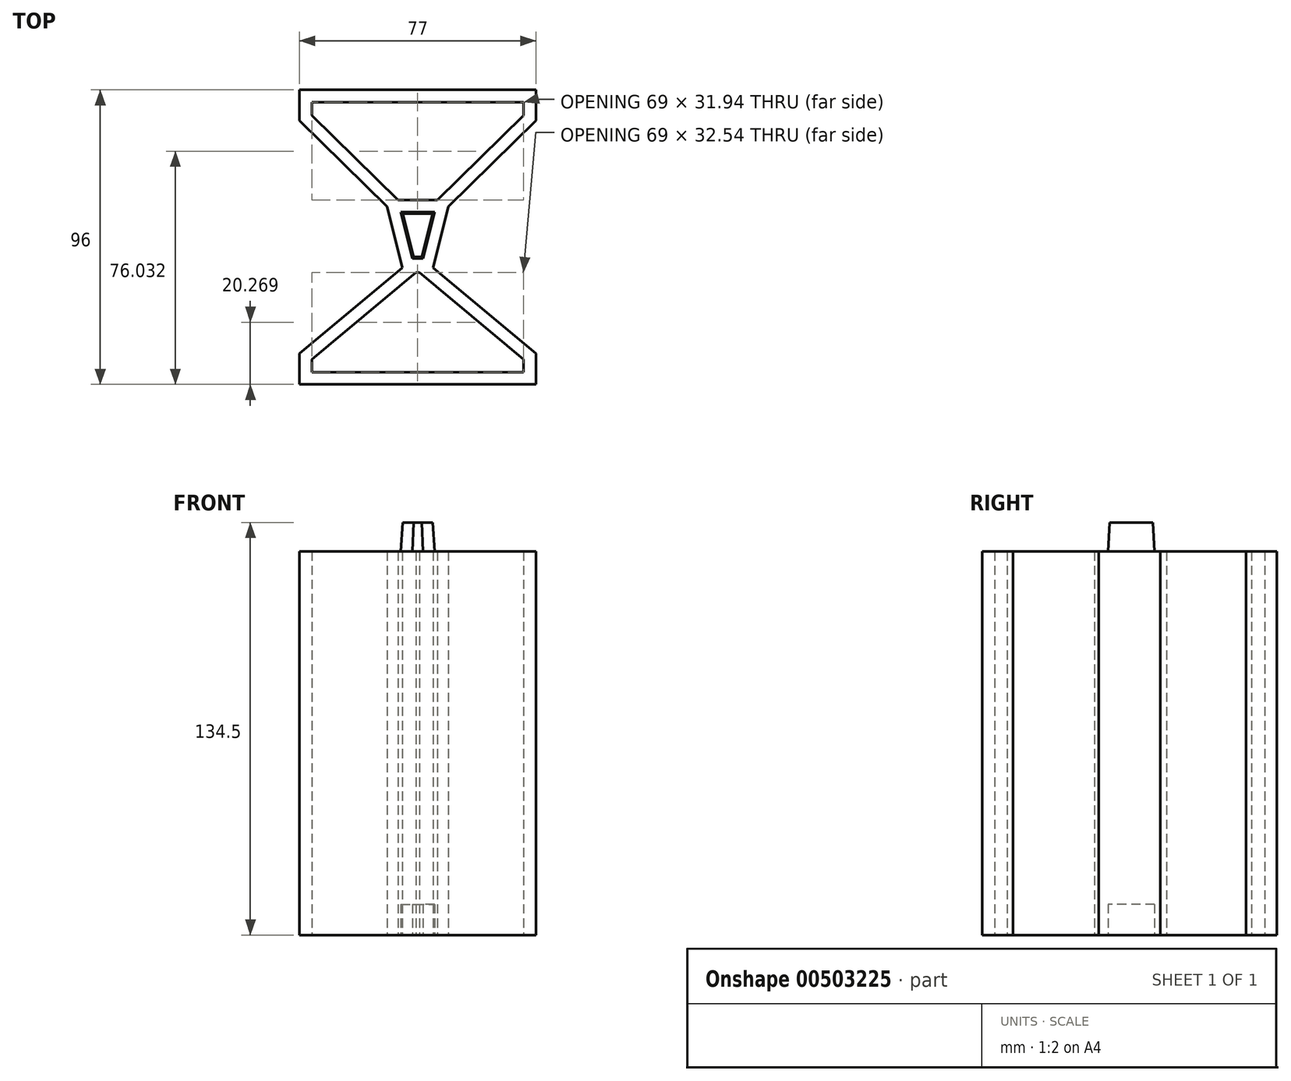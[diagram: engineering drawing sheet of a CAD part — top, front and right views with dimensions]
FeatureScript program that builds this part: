
annotation { "Feature Type Name" : "Feature", "Feature Type Description" : "" }
export const myFeature = defineFeature(function(context is Context, id is Id, definition is map)
    precondition{}
    {
        {
            var Q0;
            Q0=qCreatedBy(makeId("Top.planeOp"),FACE);
            var sketch = newSketch(context, id + "F0", { "sketchPlane" : qUnion([Q0])});
            skLineSegment(sketch, "E0", {"start": v(-38.5, -48) * mm, "end": v(38.5, -48) * mm});
            skLineSegment(sketch, "E1", {"start": v(0, -48) * mm, "end": v(0, 48) * mm, "construction": true});
            skLineSegment(sketch, "E2", {"start": v(-38.5, 48) * mm, "end": v(38.5, 48) * mm});
            skPoint(sketch, "E3", {"position": v(0, 48) * mm});
            skPoint(sketch, "E4", {"position": v(0, 0) * mm});
            skLineSegment(sketch, "E5.0", {"start": v(-38.5, -51) * mm, "end": v(38.5, -51) * mm});
            skLineSegment(sketch, "E6", {"start": v(-38.5, -51) * mm, "end": v(-38.5, -48) * mm});
            skLineSegment(sketch, "E7", {"start": v(38.5, -51) * mm, "end": v(38.5, -48) * mm});
            skLineSegment(sketch, "E8.0", {"start": v(-38.5, 51) * mm, "end": v(38.5, 51) * mm});
            skLineSegment(sketch, "E9", {"start": v(-38.5, 51) * mm, "end": v(-38.5, 48) * mm});
            skLineSegment(sketch, "E10", {"start": v(38.5, 51) * mm, "end": v(38.5, 48) * mm});
            skLineSegment(sketch, "E11", {"start": v(-38.5, -48) * mm, "end": v(-38.5, -38) * mm});
            skLineSegment(sketch, "E12", {"start": v(0, 0) * mm, "end": v(0, -10) * mm, "construction": true});
            skLineSegment(sketch, "E13", {"start": v(0, -10) * mm, "end": v(-5, -10) * mm, "construction": true});
            skLineSegment(sketch, "E14", {"start": v(-5, -10) * mm, "end": v(-38.5, -38) * mm});
            skLineSegment(sketch, "E15", {"start": v(-38.5, 48) * mm, "end": v(-38.5, 38) * mm});
            skLineSegment(sketch, "E16", {"start": v(0, 0) * mm, "end": v(0, 10) * mm, "construction": true});
            skLineSegment(sketch, "E17", {"start": v(0, 10) * mm, "end": v(-10, 10) * mm, "construction": true});
            skLineSegment(sketch, "E18", {"start": v(-10, 10) * mm, "end": v(-38.5, 38) * mm});
            skLineSegment(sketch, "E19", {"start": v(-10, 10) * mm, "end": v(-5, -10) * mm});
            skLineSegment(sketch, "E20.MirrorCS", {"start": v(38.5, 48) * mm, "end": v(38.5, 38) * mm});
            skLineSegment(sketch, "E21.MirrorCS", {"start": v(10, 10) * mm, "end": v(38.5, 38) * mm});
            skLineSegment(sketch, "E22.MirrorCS", {"start": v(10, 10) * mm, "end": v(5, -10) * mm});
            skLineSegment(sketch, "E23.MirrorCS", {"start": v(5, -10) * mm, "end": v(38.5, -38) * mm});
            skLineSegment(sketch, "E24.MirrorCS", {"start": v(38.5, -48) * mm, "end": v(38.5, -38) * mm});
            skLineSegment(sketch, "E25.1", {"start": v(0.51, -11.46) * mm, "end": v(34.5, -39.87) * mm});
            skLineSegment(sketch, "E25.2", {"start": v(34.5, -44) * mm, "end": v(34.5, -39.87) * mm});
            skLineSegment(sketch, "E25.3", {"start": v(-34.5, -44) * mm, "end": v(34.5, -44) * mm});
            skLineSegment(sketch, "E25.4", {"start": v(-34.5, -44) * mm, "end": v(-34.5, -39.87) * mm});
            skLineSegment(sketch, "E25.6", {"start": v(-0.51, -11.46) * mm, "end": v(-34.5, -39.87) * mm});
            skLineSegment(sketch, "E25.7", {"start": v(6.4, 12.06) * mm, "end": v(34.5, 39.68) * mm});
            skLineSegment(sketch, "E25.8", {"start": v(34.5, 44) * mm, "end": v(34.5, 39.68) * mm});
            skLineSegment(sketch, "E25.9", {"start": v(-34.5, 44) * mm, "end": v(34.5, 44) * mm});
            skLineSegment(sketch, "E25.10", {"start": v(-34.5, 44) * mm, "end": v(-34.5, 39.68) * mm});
            skLineSegment(sketch, "E25.11", {"start": v(-6.4, 12.06) * mm, "end": v(-34.5, 39.68) * mm});
            skLineSegment(sketch, "E26", {"start": v(-6.4, 12.06) * mm, "end": v(6.4, 12.06) * mm});
            skLineSegment(sketch, "E27", {"start": v(-0.51, -11.46) * mm, "end": v(0.51, -11.46) * mm});
            skLineSegment(sketch, "E28.1", {"start": v(5.52, 8.16) * mm, "end": v(1.74, -6.96) * mm});
            skLineSegment(sketch, "E28.3", {"start": v(-5.52, 8.16) * mm, "end": v(-1.74, -6.96) * mm});
            skLineSegment(sketch, "E28.4", {"start": v(-5.52, 8.16) * mm, "end": v(5.52, 8.16) * mm});
            skLineSegment(sketch, "E29", {"start": v(-5.52, 8.16) * mm, "end": v(-5.52, 12.06) * mm, "construction": true});
            skLineSegment(sketch, "E30", {"start": v(5.52, 8.16) * mm, "end": v(5.52, 12.06) * mm, "construction": true});
            skLineSegment(sketch, "E31", {"start": v(0, 8.16) * mm, "end": v(0, 0) * mm, "construction": true});
            skLineSegment(sketch, "E32", {"start": v(-38.5, 38) * mm, "end": v(-38.5, -38) * mm, "construction": true});
            skLineSegment(sketch, "E33", {"start": v(0, 0) * mm, "end": v(0, -11.46) * mm, "construction": true});
            skLineSegment(sketch, "E34", {"start": v(0, -11.46) * mm, "end": v(0, -44) * mm, "construction": true});
            skLineSegment(sketch, "E35", {"start": v(-1.74, -6.96) * mm, "end": v(1.74, -6.96) * mm});
            skLineSegment(sketch, "E36", {"start": v(0, 0) * mm, "end": v(0, -6.96) * mm, "construction": true});
            skSolve(sketch);
        }
        {
            var Q0;
            Q0=makeQuery(id+"F0.imprint","IMPRINT",FACE,{"disambiguationData":[TD([[makeQuery(id+"F0.imprint","IMPRINT",EDGE,{"derivedFrom":sQuery(id+"F0.wireOp",EDGE,"E0")}),1.0]])]});
            var Q1;
            Q1=makeQuery(id+"F0.imprint","IMPRINT",FACE,{"disambiguationData":[TD([[makeQuery(id+"F0.imprint","IMPRINT",EDGE,{"derivedFrom":sQuery(id+"F0.wireOp",EDGE,"E19")}),1.0]])]});
            var Q2;
            Q2=makeQuery(id+"F0.imprint","IMPRINT",FACE,{"disambiguationData":[TD([[makeQuery(id+"F0.imprint","IMPRINT",EDGE,{"derivedFrom":sQuery(id+"F0.wireOp",EDGE,"E2")}),-1.0]])]});
            var Q3;
            Q3=makeQuery(id+"F0.imprint","IMPRINT",FACE,{"disambiguationData":[TD([[makeQuery(id+"F0.imprint","IMPRINT",EDGE,{"derivedFrom":sQuery(id+"F0.wireOp",EDGE,"E28.0")}),-1.0]])]});
            var Q4;
            Q4=makeQuery(id+"F0.imprint","IMPRINT",FACE,{"disambiguationData":[TD([[makeQuery(id+"F0.imprint","IMPRINT",EDGE,{"derivedFrom":sQuery(id+"F0.wireOp",EDGE,"E28.1")}),-1.0]])]});
            extrude(context, id + "F1", {"entities" : qUnion([Q0, Q1, Q2, Q3, Q4]), "depth" : 125 * mm});
        }
        {
            var Q0;
            Q0=makeQuery(id+"F0.imprint","IMPRINT",FACE,{"disambiguationData":[TD([[makeQuery(id+"F0.imprint","IMPRINT",EDGE,{"derivedFrom":sQuery(id+"F0.wireOp",EDGE,"E28.0")}),-1.0]])]});
            var Q1;
            Q1=makeQuery(id+"F0.imprint","IMPRINT",FACE,{"disambiguationData":[TD([[makeQuery(id+"F0.imprint","IMPRINT",EDGE,{"derivedFrom":sQuery(id+"F0.wireOp",EDGE,"E28.1")}),-1.0]])]});
            extrude(context, id + "F2", {"entities" : qUnion([Q0, Q1]), "operationType" : NewBodyOperationType.REMOVE, "depth" : 10 * mm});
        }
        {
            var Q0;
            Q0=makeQuery(id+"F1.opExtrude","CAP_FACE",FACE,{"disambiguationData":[OSD([sQuery(id+"F0.wireOp",EDGE,"E0"),sQuery(id+"F0.wireOp",EDGE,"E2"),sQuery(id+"F0.wireOp",EDGE,"E11"),sQuery(id+"F0.wireOp",EDGE,"E14"),sQuery(id+"F0.wireOp",EDGE,"E15"),sQuery(id+"F0.wireOp",EDGE,"E18"),sQuery(id+"F0.wireOp",EDGE,"E19"),sQuery(id+"F0.wireOp",EDGE,"E20.MirrorCS"),sQuery(id+"F0.wireOp",EDGE,"E21.MirrorCS"),sQuery(id+"F0.wireOp",EDGE,"E22.MirrorCS"),sQuery(id+"F0.wireOp",EDGE,"E23.MirrorCS"),sQuery(id+"F0.wireOp",EDGE,"E24.MirrorCS"),sQuery(id+"F0.wireOp",EDGE,"E25.1"),sQuery(id+"F0.wireOp",EDGE,"E25.2"),sQuery(id+"F0.wireOp",EDGE,"E25.3"),sQuery(id+"F0.wireOp",EDGE,"E25.4"),sQuery(id+"F0.wireOp",EDGE,"E25.6"),sQuery(id+"F0.wireOp",EDGE,"E25.7"),sQuery(id+"F0.wireOp",EDGE,"E25.8"),sQuery(id+"F0.wireOp",EDGE,"E25.9"),sQuery(id+"F0.wireOp",EDGE,"E25.10"),sQuery(id+"F0.wireOp",EDGE,"E25.11"),sQuery(id+"F0.wireOp",EDGE,"E26"),sQuery(id+"F0.wireOp",EDGE,"E27")])],"isStart":false});
            var sketch = newSketch(context, id + "F3", { "sketchPlane" : qUnion([Q0])});
            skLineSegment(sketch, "E37", {"start": v(-38.5, -48) * mm, "end": v(38.5, -48) * mm});
            skLineSegment(sketch, "E38", {"start": v(0, -48) * mm, "end": v(0, 48) * mm, "construction": true});
            skLineSegment(sketch, "E39", {"start": v(-38.5, 48) * mm, "end": v(38.5, 48) * mm});
            skPoint(sketch, "E40", {"position": v(0, 48) * mm});
            skPoint(sketch, "E41", {"position": v(0, 0) * mm});
            skLineSegment(sketch, "E42.0", {"start": v(-38.5, -51) * mm, "end": v(38.5, -51) * mm});
            skLineSegment(sketch, "E43", {"start": v(-38.5, -51) * mm, "end": v(-38.5, -48) * mm});
            skLineSegment(sketch, "E44", {"start": v(38.5, -51) * mm, "end": v(38.5, -48) * mm});
            skLineSegment(sketch, "E45.0", {"start": v(-38.5, 51) * mm, "end": v(38.5, 51) * mm});
            skLineSegment(sketch, "E46", {"start": v(-38.5, 51) * mm, "end": v(-38.5, 48) * mm});
            skLineSegment(sketch, "E47", {"start": v(38.5, 51) * mm, "end": v(38.5, 48) * mm});
            skLineSegment(sketch, "E48", {"start": v(-38.5, -48) * mm, "end": v(-38.5, -38) * mm});
            skLineSegment(sketch, "E49", {"start": v(0, 0) * mm, "end": v(0, -10) * mm, "construction": true});
            skLineSegment(sketch, "E50", {"start": v(0, -10) * mm, "end": v(-5, -10) * mm, "construction": true});
            skLineSegment(sketch, "E51", {"start": v(-5, -10) * mm, "end": v(-38.5, -38) * mm});
            skLineSegment(sketch, "E52", {"start": v(-38.5, 48) * mm, "end": v(-38.5, 38) * mm});
            skLineSegment(sketch, "E53", {"start": v(0, 0) * mm, "end": v(0, 10) * mm, "construction": true});
            skLineSegment(sketch, "E54", {"start": v(0, 10) * mm, "end": v(-10, 10) * mm, "construction": true});
            skLineSegment(sketch, "E55", {"start": v(-10, 10) * mm, "end": v(-38.5, 38) * mm});
            skLineSegment(sketch, "E56", {"start": v(-10, 10) * mm, "end": v(-5, -10) * mm});
            skLineSegment(sketch, "E57.MirrorCS", {"start": v(38.5, 48) * mm, "end": v(38.5, 38) * mm});
            skLineSegment(sketch, "E58.MirrorCS", {"start": v(10, 10) * mm, "end": v(38.5, 38) * mm});
            skLineSegment(sketch, "E59.MirrorCS", {"start": v(10, 10) * mm, "end": v(5, -10) * mm});
            skLineSegment(sketch, "E60.MirrorCS", {"start": v(5, -10) * mm, "end": v(38.5, -38) * mm});
            skLineSegment(sketch, "E61.MirrorCS", {"start": v(38.5, -48) * mm, "end": v(38.5, -38) * mm});
            skLineSegment(sketch, "E62.1", {"start": v(0.51, -11.46) * mm, "end": v(34.5, -39.87) * mm});
            skLineSegment(sketch, "E62.2", {"start": v(34.5, -44) * mm, "end": v(34.5, -39.87) * mm});
            skLineSegment(sketch, "E62.3", {"start": v(-34.5, -44) * mm, "end": v(34.5, -44) * mm});
            skLineSegment(sketch, "E62.4", {"start": v(-34.5, -44) * mm, "end": v(-34.5, -39.87) * mm});
            skLineSegment(sketch, "E62.6", {"start": v(-0.51, -11.46) * mm, "end": v(-34.5, -39.87) * mm});
            skLineSegment(sketch, "E62.7", {"start": v(6.4, 12.06) * mm, "end": v(34.5, 39.68) * mm});
            skLineSegment(sketch, "E62.8", {"start": v(34.5, 44) * mm, "end": v(34.5, 39.68) * mm});
            skLineSegment(sketch, "E62.9", {"start": v(-34.5, 44) * mm, "end": v(34.5, 44) * mm});
            skLineSegment(sketch, "E62.10", {"start": v(-34.5, 44) * mm, "end": v(-34.5, 39.68) * mm});
            skLineSegment(sketch, "E62.11", {"start": v(-6.4, 12.06) * mm, "end": v(-34.5, 39.68) * mm});
            skLineSegment(sketch, "E63", {"start": v(-6.4, 12.06) * mm, "end": v(6.4, 12.06) * mm});
            skLineSegment(sketch, "E64", {"start": v(-0.51, -11.46) * mm, "end": v(0.51, -11.46) * mm});
            skLineSegment(sketch, "E65.1", {"start": v(5.52, 8.16) * mm, "end": v(1.74, -6.96) * mm});
            skLineSegment(sketch, "E65.3", {"start": v(-5.52, 8.16) * mm, "end": v(-1.74, -6.96) * mm});
            skLineSegment(sketch, "E65.4", {"start": v(-5.52, 8.16) * mm, "end": v(5.52, 8.16) * mm});
            skLineSegment(sketch, "E66", {"start": v(-5.52, 8.16) * mm, "end": v(-5.52, 12.06) * mm, "construction": true});
            skLineSegment(sketch, "E67", {"start": v(5.52, 8.16) * mm, "end": v(5.52, 12.06) * mm, "construction": true});
            skLineSegment(sketch, "E68", {"start": v(0, 8.16) * mm, "end": v(0, 0) * mm, "construction": true});
            skLineSegment(sketch, "E69", {"start": v(-38.5, 38) * mm, "end": v(-38.5, -38) * mm, "construction": true});
            skLineSegment(sketch, "E70", {"start": v(0, 0) * mm, "end": v(0, -11.46) * mm, "construction": true});
            skLineSegment(sketch, "E71", {"start": v(0, -11.46) * mm, "end": v(0, -44) * mm, "construction": true});
            skLineSegment(sketch, "E72", {"start": v(-1.74, -6.96) * mm, "end": v(1.74, -6.96) * mm});
            skLineSegment(sketch, "E73", {"start": v(0, 0) * mm, "end": v(0, -6.96) * mm, "construction": true});
            skSolve(sketch);
        }
        {
            var Q0;
            Q0=makeQuery(id+"F3.imprint","IMPRINT",FACE,{"disambiguationData":[TD([[makeQuery(id+"F3.imprint","IMPRINT",EDGE,{"derivedFrom":sQuery(id+"F3.wireOp",EDGE,"E65.1")}),-1.0]])]});
            extrude(context, id + "F4", {"entities" : qUnion([Q0]), "operationType" : NewBodyOperationType.ADD, "depth" : 9.5 * mm});
        }
        {
            var Q0;
            Q0=makeQuery(id+"F4.opExtrude","CAP_EDGE",EDGE,{"disambiguationData":[OSD([sQuery(id+"F3.wireOp",EDGE,"E65.1")])],"isStart":false});
            var Q1;
            Q1=makeQuery(id+"F4.opExtrude","CAP_EDGE",EDGE,{"disambiguationData":[OSD([sQuery(id+"F3.wireOp",EDGE,"E72")])],"isStart":false});
            var Q2;
            Q2=makeQuery(id+"F4.opExtrude","CAP_EDGE",EDGE,{"disambiguationData":[OSD([sQuery(id+"F3.wireOp",EDGE,"E65.3")])],"isStart":false});
            var Q3;
            Q3=makeQuery(id+"F4.opExtrude","CAP_EDGE",EDGE,{"disambiguationData":[OSD([sQuery(id+"F3.wireOp",EDGE,"E65.4")])],"isStart":false});
            chamfer(context, id + "F5", {"entities" : qUnion([Q0, Q1, Q2, Q3]), "chamferType" : ChamferType.TWO_OFFSETS, "width1" : 10 * mm, "oppositeDirection" : false, "width2" : .5 * mm, "tangentPropagation" : true});
        }
    });
